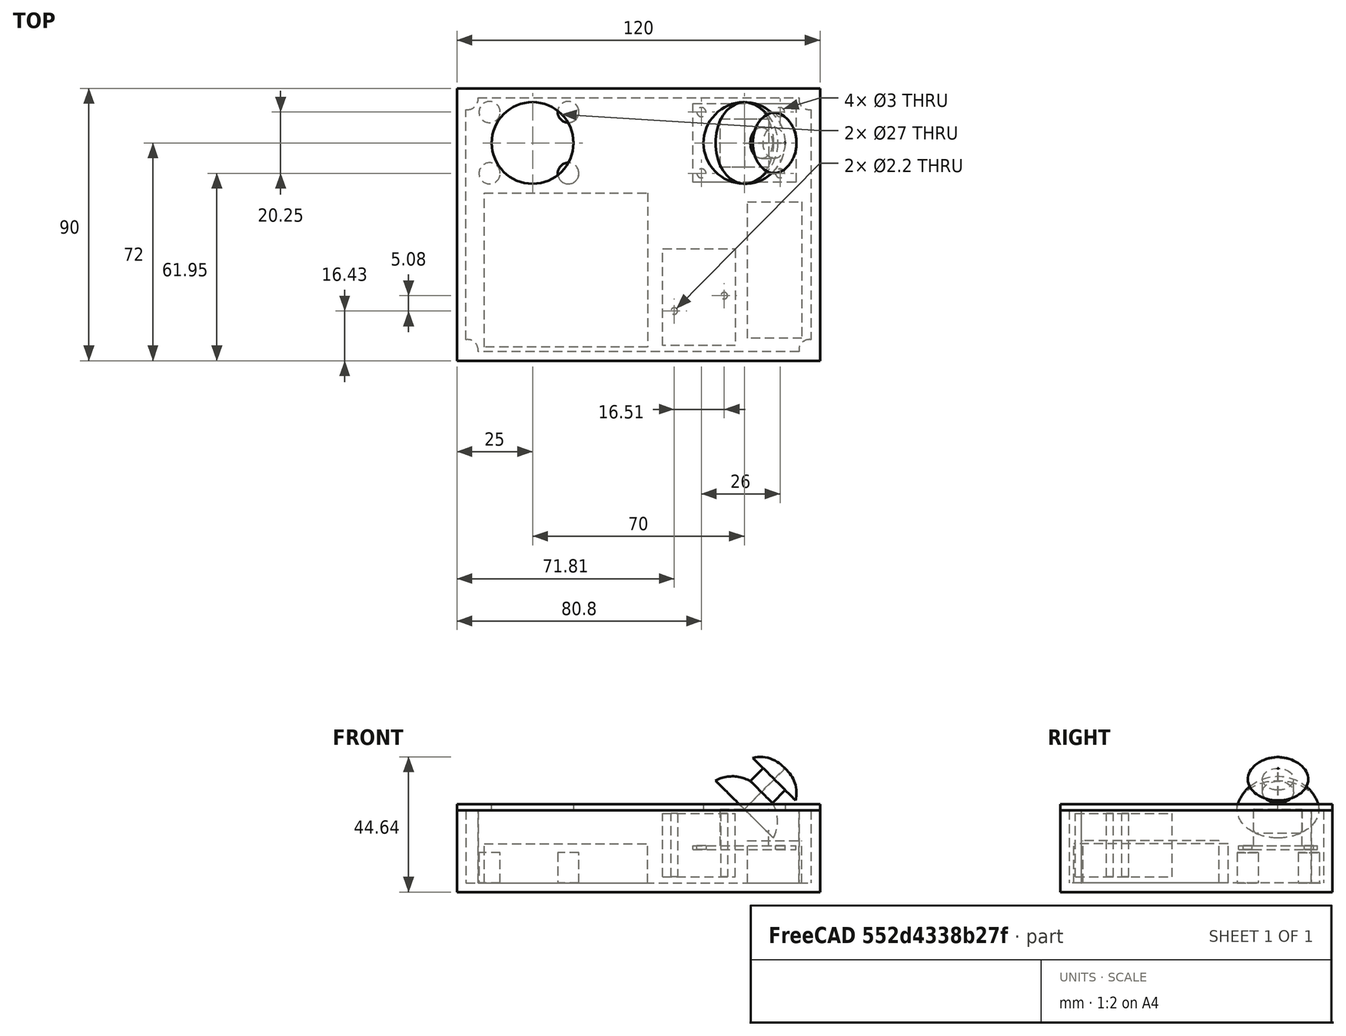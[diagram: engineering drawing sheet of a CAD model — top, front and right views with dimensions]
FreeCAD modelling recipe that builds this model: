
FCSTD DOCUMENT  (FreeCAD 0.18.4R)
Label: bottom
License: All rights reserved
LicenseURL: http://en.wikipedia.org/wiki/All_rights_reserved
objects: Sketcher::SketchObject×15, PartDesign::Pad×10, PartDesign::Body×7, PartDesign::ShapeBinder×6, TechDraw::DrawViewDimension×6, PartDesign::Pocket×4, TechDraw::DrawSVGTemplate×2, TechDraw::DrawViewPart×2, TechDraw::DrawPage×2, PartDesign::Plane×1, PartDesign::Revolution×1, PartDesign::FeatureBase×1
note: 60 computed .brp shape members not serialized (recipe doc carries the construction recipe); baked Part::Feature solids carry a one-line shape summary decoded from their .brp

FEATURE [PartDesign::Plane] DatumPlane
  Length = 140.785
  MapMode = 6
  ResizeMode = 0
  Width = 110.785
FEATURE [Sketcher::SketchObject] Sketch  label="body"
  MapMode = 5
  Support = -> [DatumPlane]
  sketch-geometry (7):
    g0: LineSegment StartX=-60 StartY=45 StartZ=0 EndX=60 EndY=45 EndZ=0
    g1: LineSegment StartX=60 StartY=45 StartZ=0 EndX=60 EndY=-45 EndZ=0
    g2: LineSegment StartX=60 StartY=-45 StartZ=0 EndX=-60 EndY=-45 EndZ=0
    g3: LineSegment StartX=-60 StartY=-45 StartZ=0 EndX=-60 EndY=45 EndZ=0
    g4: LineSegment [constr] StartX=-60 StartY=45 StartZ=0 EndX=60 EndY=-45 EndZ=0
    g5: LineSegment [constr] StartX=60 StartY=45 StartZ=0 EndX=-60 EndY=-45 EndZ=0
    g6: GeomPoint X=0 Y=0 Z=0
  constraints (17):
    c: Coincident(g0,g1)
    c: Coincident(g1,g2)
    c: Coincident(g2,g3)
    c: Coincident(g3,g0)
    c: Horizontal(g0)
    c: Horizontal(g2)
    c: Vertical(g1)
    c: Vertical(g3)
    c: DistanceX(g0,g0) = 120
    c: Coincident(g4,g1)
    c: Coincident(g5,g0)
    c: Coincident(g5,g2)
    c: PointOnObject(g6,g4)
    c: PointOnObject(g6,g5)
    c: Coincident(g6,g-1)
    c: DistanceY(g1,g1) = 90
    c: Coincident(g0,g4)
FEATURE [PartDesign::Pad] Pad
  Length = 27
  Length2 = 100
  Profile = -> Sketch
  Type = 0
FEATURE [Sketcher::SketchObject] Sketch001  label="hole"
  ExternalGeometry = -> [Sketch,Pad]
  MapMode = 5
  Placement = pos=(0,0,27) rot=(0,0,1;0rad)
  Support = -> [Pad]
  sketch-geometry (19):
    g0: LineSegment [constr] StartX=-60 StartY=45 StartZ=0 EndX=60 EndY=45 EndZ=0
    g1: LineSegment [constr] StartX=60 StartY=-45 StartZ=0 EndX=-60 EndY=-45 EndZ=0
    g2: LineSegment [constr] StartX=-60 StartY=-45 StartZ=0 EndX=-60 EndY=45 EndZ=0
    g3: Circle [constr] CenterX=-56.5 CenterY=41.5 CenterZ=0 NormalX=0 NormalY=0 NormalZ=1 AngleXU=0 Radius=3.5
    g4: Circle [constr] CenterX=56.5 CenterY=41.5 CenterZ=0 NormalX=0 NormalY=0 NormalZ=1 AngleXU=0 Radius=3.5
    g5: Circle [constr] CenterX=56.5 CenterY=-41.5 CenterZ=0 NormalX=0 NormalY=0 NormalZ=1 AngleXU=0 Radius=3.5
    g6: Circle [constr] CenterX=-56.5 CenterY=-41.5 CenterZ=0 NormalX=0 NormalY=0 NormalZ=1 AngleXU=0 Radius=3.5
    g7: LineSegment [constr] StartX=-57 StartY=42 StartZ=0 EndX=57 EndY=42 EndZ=0
    g8: LineSegment [constr] StartX=57 StartY=42 StartZ=0 EndX=57 EndY=-42 EndZ=0
    g9: LineSegment [constr] StartX=57 StartY=-42 StartZ=0 EndX=-57 EndY=-42 EndZ=0
    g10: LineSegment [constr] StartX=-57 StartY=-42 StartZ=0 EndX=-57 EndY=42 EndZ=0
    g11: ArcOfCircle CenterX=-56.5 CenterY=41.5 CenterZ=0 NormalX=0 NormalY=0 NormalZ=1 AngleXU=0 Radius=3.5 StartAngle=4.56904 EndAngle=6.42653
    g12: ArcOfCircle CenterX=56.5 CenterY=41.5 CenterZ=0 NormalX=0 NormalY=0 NormalZ=1 AngleXU=0 Radius=3.5 StartAngle=2.99825 EndAngle=4.85574
    g13: ArcOfCircle CenterX=56.5 CenterY=-41.5 CenterZ=0 NormalX=0 NormalY=0 NormalZ=1 AngleXU=0 Radius=3.5 StartAngle=1.42745 EndAngle=3.28494
    g14: LineSegment StartX=-53.0359 StartY=42 StartZ=0 EndX=53.0359 EndY=42 EndZ=0
    g15: LineSegment StartX=57 StartY=38.0359 StartZ=0 EndX=57 EndY=-38.0359 EndZ=0
    g16: ArcOfCircle CenterX=-56.5 CenterY=-41.5 CenterZ=0 NormalX=0 NormalY=0 NormalZ=1 AngleXU=0 Radius=3.5 StartAngle=6.13984 EndAngle=7.99733
    g17: LineSegment StartX=53.0359 StartY=-42 StartZ=0 EndX=-53.0359 EndY=-42 EndZ=0
    g18: LineSegment StartX=-57 StartY=-38.0359 StartZ=0 EndX=-57 EndY=38.0359 EndZ=0
  constraints (56):
    c: Coincident(g1,g2)
    c: Coincident(g2,g0)
    c: Tangent(g0,g3)
    c: Tangent(g3,g2)
    c: Radius(g3) = 3.5
    c: Tangent(g0,g4)
    c: Radius(g4) = 3.5
    c: Tangent(g5,g1)
    c: Radius(g5) = 3.5
    c: Radius(g6) = 3.5
    c: Tangent(g6,g1)
    c: Tangent(g6,g2)
    c: Coincident(g7,g8)
    c: Coincident(g8,g9)
    c: Coincident(g9,g10)
    c: Coincident(g10,g7)
    c: Horizontal(g7)
    c: Horizontal(g9)
    c: Vertical(g8)
    c: Vertical(g10)
    c: DistanceX(g0,g7) = 3
    c: DistanceY(g7,g0) = 3
    c: DistanceX(g8,g1) = 3
    c: DistanceY(g1,g8) = 3
    c: Coincident(g11,g3)
    c: PointOnObject(g11,g10)
    c: Coincident(g12,g4)
    c: PointOnObject(g12,g7)
    c: PointOnObject(g12,g8)
    c: Coincident(g13,g5)
    c: PointOnObject(g13,g8)
    c: PointOnObject(g13,g9)
    c: Radius(g11) = 3.5
    c: Radius(g12) = 3.5
    c: Radius(g13) = 3.5
    c: Coincident(g14,g11)
    c: Coincident(g14,g12)
    c: Horizontal(g14)
    c: Coincident(g15,g12)
    c: Coincident(g15,g13)
    c: Coincident(g16,g6)
    c: PointOnObject(g16,g10)
    c: PointOnObject(g16,g9)
    c: Coincident(g17,g13)
    c: Coincident(g17,g16)
    c: Coincident(g18,g16)
    c: Coincident(g18,g11)
    c: Radius(g16) = 3.5
    c: DistanceX(g12,g-3) = 3
    c: Coincident(g0,g-3)
    c: Coincident(g-3,g0)
    c: Tangent(g4,g-5)
    c: Coincident(g1,g-4)
    c: Coincident(g1,g-5)
    c: Coincident(g1,g-4)
    c: Tangent(g5,g-5)
FEATURE [PartDesign::Pocket] Pocket
  BaseFeature = -> Pad
  Length = 24
  Length2 = 100
  Profile = -> Sketch001
  Type = 0
FEATURE [Sketcher::SketchObject] Sketch006  label="pcb"
  MapMode = 5
  Support = -> [XY_Plane002]
  sketch-geometry (7):
    g0: LineSegment StartX=-17 StartY=13 StartZ=0 EndX=17 EndY=13 EndZ=0
    g1: LineSegment StartX=17 StartY=13 StartZ=0 EndX=17 EndY=-13 EndZ=0
    g2: LineSegment StartX=17 StartY=-13 StartZ=0 EndX=-17 EndY=-13 EndZ=0
    g3: LineSegment StartX=-17 StartY=-13 StartZ=0 EndX=-17 EndY=13 EndZ=0
    g4: LineSegment [constr] StartX=17 StartY=13 StartZ=0 EndX=-17 EndY=-13 EndZ=0
    g5: LineSegment [constr] StartX=-17 StartY=13 StartZ=0 EndX=17 EndY=-13 EndZ=0
    g6: GeomPoint X=0 Y=0 Z=0
  constraints (17):
    c: Coincident(g0,g1)
    c: Coincident(g1,g2)
    c: Coincident(g2,g3)
    c: Coincident(g3,g0)
    c: Horizontal(g0)
    c: Horizontal(g2)
    c: Vertical(g1)
    c: Vertical(g3)
    c: DistanceX(g0,g0) = 34
    c: DistanceY(g1,g1) = 26
    c: Coincident(g4,g0)
    c: Coincident(g4,g2)
    c: Coincident(g5,g0)
    c: Coincident(g5,g1)
    c: PointOnObject(g6,g4)
    c: PointOnObject(g6,g5)
    c: Coincident(g6,g-1)
FEATURE [PartDesign::Pad] Pad004
  Length = 1.35
  Length2 = 100
  Profile = -> Sketch006
  Type = 0
FEATURE [Sketcher::SketchObject] Sketch007  label="mounting_holes"
  ExternalGeometry = -> [Pad004]
  MapMode = 5
  Placement = pos=(0,0,1.35) rot=(0,0,1;0rad)
  Support = -> [Pad004]
  sketch-geometry (11):
    g0: Circle CenterX=-14.2 CenterY=10.2 CenterZ=0 NormalX=0 NormalY=0 NormalZ=1 AngleXU=0 Radius=1.5
    g1: Circle CenterX=11.8 CenterY=10.2 CenterZ=0 NormalX=0 NormalY=0 NormalZ=1 AngleXU=0 Radius=1.5
    g2: Circle CenterX=11.8 CenterY=-10.05 CenterZ=0 NormalX=0 NormalY=0 NormalZ=1 AngleXU=0 Radius=1.5
    g3: Circle CenterX=-14.2 CenterY=-10.05 CenterZ=0 NormalX=0 NormalY=0 NormalZ=1 AngleXU=0 Radius=1.5
    g4: LineSegment [constr] StartX=-15.7 StartY=13 StartZ=0 EndX=-15.7 EndY=-13 EndZ=0
    g5: LineSegment [constr] StartX=13.3 StartY=13 StartZ=0 EndX=13.3 EndY=-13 EndZ=0
    g6: LineSegment [constr] StartX=-15.7 StartY=-11.55 StartZ=0 EndX=13.3 EndY=-11.55 EndZ=0
    g7: LineSegment [constr] StartX=-15.7 StartY=11.7 StartZ=0 EndX=13.3 EndY=11.7 EndZ=0
    g8: GeomPoint X=0 Y=0 Z=0
    g9: LineSegment [constr] StartX=-17 StartY=13 StartZ=0 EndX=17 EndY=-13 EndZ=0
    g10: LineSegment [constr] StartX=17 StartY=13 StartZ=0 EndX=-17 EndY=-13 EndZ=0
  constraints (33):
    c: Diameter(g0) = 3
    c: Equal(g0,g1) = 3
    c: Equal(g0,g2) = 3
    c: Equal(g0,g3) = 3
    c: PointOnObject(g4,g-3)
    c: PointOnObject(g4,g-5)
    c: Vertical(g4)
    c: PointOnObject(g5,g-3)
    c: PointOnObject(g5,g-5)
    c: Vertical(g5)
    c: Tangent(g1,g5)
    c: Tangent(g2,g5)
    c: Tangent(g0,g4)
    c: Tangent(g3,g4)
    c: DistanceX(g4,g5) = 29
    c: PointOnObject(g6,g4)
    c: PointOnObject(g6,g5)
    c: Horizontal(g6)
    c: Tangent(g6,g3)
    c: PointOnObject(g7,g4)
    c: PointOnObject(g7,g5)
    c: Horizontal(g7)
    c: Tangent(g7,g0)
    c: Tangent(g1,g7)
    c: Tangent(g2,g6)
    c: DistanceY(g6,g7) = 23.25
    c: Coincident(g8,g-1)
    c: Coincident(g9,g-6)
    c: Coincident(g9,g-5)
    c: Coincident(g10,g-4)
    c: Coincident(g10,g-6)
    c: DistanceY(g7,g4) = 1.3
    c: DistanceX(g9,g7) = 1.3
FEATURE [PartDesign::Pocket] Pocket002
  BaseFeature = -> Pad004
  Length = 1.35
  Length2 = 100
  Profile = -> Sketch007
  Type = 0
FEATURE [Sketcher::SketchObject] Sketch008  label="potis"
  MapMode = 5
  Placement = pos=(0,0,1.35) rot=(0,0,1;0rad)
  Support = -> [Pocket002]
  sketch-geometry (7):
    g0: LineSegment StartX=-8 StartY=8 StartZ=0 EndX=8 EndY=8 EndZ=0
    g1: LineSegment StartX=8 StartY=8 StartZ=0 EndX=8 EndY=-8 EndZ=0
    g2: LineSegment StartX=8 StartY=-8 StartZ=0 EndX=-8 EndY=-8 EndZ=0
    g3: LineSegment StartX=-8 StartY=-8 StartZ=0 EndX=-8 EndY=8 EndZ=0
    g4: LineSegment [constr] StartX=-8 StartY=8 StartZ=0 EndX=8 EndY=-8 EndZ=0
    g5: LineSegment [constr] StartX=-8 StartY=-8 StartZ=0 EndX=8 EndY=8 EndZ=0
    g6: GeomPoint X=0 Y=0 Z=0
  constraints (17):
    c: Coincident(g0,g1)
    c: Coincident(g1,g2)
    c: Coincident(g2,g3)
    c: Coincident(g3,g0)
    c: Horizontal(g0)
    c: Horizontal(g2)
    c: Vertical(g1)
    c: Vertical(g3)
    c: DistanceX(g0,g0) = 16
    c: Equal(g0,g1)
    c: Coincident(g4,g0)
    c: Coincident(g4,g1)
    c: Coincident(g5,g2)
    c: Coincident(g5,g0)
    c: PointOnObject(g6,g4)
    c: PointOnObject(g6,g5)
    c: Coincident(g6,g-1)
FEATURE [PartDesign::Pad] Pad005
  BaseFeature = -> Pocket002
  Length = 12
  Length2 = 100
  Profile = -> Sketch008
  Type = 0
FEATURE [Sketcher::SketchObject] Sketch009  label="joy_hat"
  AttachmentOffset = pos=(0,0,0) rot=(1,0,0;1.5708rad)
  ExternalGeometry = -> [Pad005]
  MapMode = 2
  Placement = pos=(0,0,13.35) rot=(0.862856,0.357407,-0.357407;1.71777rad)
  sketch-geometry (11):
    g0: LineSegment StartX=0 StartY=0 StartZ=0 EndX=13.4918 EndY=0.0716788 EndZ=0
    g1: LineSegment [constr] StartX=0 StartY=0 StartZ=0 EndX=-0.0425023 EndY=8 EndZ=0
    g2: LineSegment [constr] StartX=-0.0425023 StartY=8 StartZ=0 EndX=5.0875 EndY=8.02725 EndZ=0
    g3: LineSegment StartX=5.0875 StartY=8.02725 StartZ=0 EndX=5.05562 EndY=14.0273 EndZ=0
    g4: LineSegment [constr] StartX=-0.074379 StartY=14 StartZ=0 EndX=9.92562 EndY=14.0531 EndZ=0
    g5: LineSegment [constr] StartX=-0.0425023 StartY=8 StartZ=0 EndX=-0.074379 EndY=14 EndZ=0
    g6: LineSegment [constr] StartX=-0.074379 StartY=14 StartZ=0 EndX=0 EndY=19 EndZ=0
    g7: LineSegment StartX=5.05562 StartY=14.0273 StartZ=0 EndX=9.92562 EndY=14.0531 EndZ=0
    g8: ArcOfCircle CenterX=0.937498 CenterY=8.45 CenterZ=0 NormalX=0 NormalY=0 NormalZ=1 AngleXU=0 Radius=10.5916 StartAngle=0.557442 EndAngle=1.65943
    g9: ArcOfCircle CenterX=2.2 CenterY=-3.44 CenterZ=0 NormalX=0 NormalY=0 NormalZ=1 AngleXU=0 Radius=11.8252 StartAngle=0.301513 EndAngle=1.32412
    g10: LineSegment StartX=0 StartY=19 StartZ=0 EndX=0 EndY=0 EndZ=0
  constraints (31):
    c: Coincident(g3,g7)
    c: Perpendicular(g0,g1)
    c: DistanceY(g1,g1) = 8
    c: DistanceY(g5,g5) = 6
    c: DistanceY(g6,g6) = 5
    c: Perpendicular(g3,g4)
    c: DistanceX(g2,g2) = 5.13
    c: DistanceX(g4,g4) = 10
    c: Perpendicular(g2,g1)
    c: Coincident(g1,g2)
    c: Coincident(g1,g5)
    c: Coincident(g4,g5)
    c: Coincident(g4,g6)
    c: Coincident(g4,g7)
    c: Coincident(g0,g1)
    c: Perpendicular(g7,g3)
    c: Coincident(g8,g6)
    c: Coincident(g8,g7)
    c: Coincident(g9,g3)
    c: Coincident(g9,g0)
    c: Coincident(g2,g3)
    c: Perpendicular(g3,g2)
    c: DistanceY(g9,g0) = 3.44
    c: DistanceX(g0,g9) = 2.2
    c: DistanceX(g1,g8) = 0.98
    c: DistanceY(g1,g8) = 0.45
    c: Coincident(g0,g-1)
    c: Perpendicular(g5,g2)
    c: Vertical(g10)
    c: Coincident(g10,g8)
    c: Coincident(g0,g10)
FEATURE [PartDesign::Revolution] Revolution
  Angle = 360
  Axis = (5.6268,1.6e-15,5.68691)
  Base = (0,0,13.35)
  BaseFeature = -> Pad005
  Profile = -> Sketch009
  ReferenceAxis = -> Sketch009 [Axis0]
  Reversed = true
FEATURE [PartDesign::Body] Body002  label="joy_left_orig"
  Group = -> [Sketch006,Pad004,Sketch007,Pocket002,Sketch008,Pad005,Sketch009,Revolution]
  Origin = -> Origin002
  Placement = pos=(-35,27,14) rot=(0,0,1;0rad)
  Tip = -> Revolution
FEATURE [PartDesign::ShapeBinder] ShapeBinder  label="shapebinder_pcb_holes_joy_left"
  Placement = pos=(-35,27,14) rot=(0,0,1;0rad)
  Support = -> [Pocket002]
  TraceSupport = true
FEATURE [Sketcher::SketchObject] Sketch010  label="mounts_joy_left"
  ExternalGeometry = -> [ShapeBinder]
  MapMode = 5
  Placement = pos=(0,0,3) rot=(0,0,1;0rad)
  Support = -> [Pocket]
  sketch-geometry (4):
    g0: Circle CenterX=-49.2 CenterY=37.2 CenterZ=0 NormalX=0 NormalY=0 NormalZ=1 AngleXU=0 Radius=3.5
    g1: Circle CenterX=-23.2 CenterY=37.2 CenterZ=0 NormalX=0 NormalY=0 NormalZ=1 AngleXU=0 Radius=3.5
    g2: Circle CenterX=-23.2 CenterY=16.95 CenterZ=0 NormalX=0 NormalY=0 NormalZ=1 AngleXU=0 Radius=3.5
    g3: Circle CenterX=-49.2 CenterY=16.95 CenterZ=0 NormalX=0 NormalY=0 NormalZ=1 AngleXU=0 Radius=3.5
  constraints (8):
    c: Diameter(g0) = 7
    c: Coincident(g0,g-3)
    c: Equal(g0,g1) = 7
    c: Coincident(g1,g-4)
    c: Equal(g0,g2) = 7
    c: Coincident(g2,g-5)
    c: Equal(g0,g3) = 7
    c: Coincident(g3,g-6)
FEATURE [PartDesign::Pad] Pad006
  BaseFeature = -> Pocket
  Length = 10
  Length2 = 100
  Profile = -> Sketch010
  Type = 0
FEATURE [PartDesign::FeatureBase] Clone
  BaseFeature = -> Body002
  Placement = pos=(0,0,9) rot=(0,0,1;0rad)
FEATURE [PartDesign::Body] Body003  label="joy_right_cloned"
  BaseFeature = -> Body002
  Group = -> [Clone]
  Origin = -> Origin003
  Placement = pos=(35,27,5) rot=(0,0,1;0rad)
  Tip = -> Clone
FEATURE [PartDesign::ShapeBinder] ShapeBinder001  label="shapebinder_pcb_holes_joy_right"
  Placement = pos=(35,27,5) rot=(0,0,1;0rad)
  Support = -> [Clone]
  TraceSupport = true
FEATURE [Sketcher::SketchObject] Sketch011  label="mounts_joy_right"
  ExternalGeometry = -> [ShapeBinder001]
  MapMode = 5
  Placement = pos=(0,0,3) rot=(0,0,1;0rad)
  Support = -> [Pad006]
  sketch-geometry (4):
    g0: Circle CenterX=20.8 CenterY=37.2 CenterZ=0 NormalX=0 NormalY=0 NormalZ=1 AngleXU=0 Radius=3.5
    g1: Circle CenterX=46.8 CenterY=37.2 CenterZ=0 NormalX=0 NormalY=0 NormalZ=1 AngleXU=0 Radius=3.5
    g2: Circle CenterX=46.8 CenterY=16.95 CenterZ=0 NormalX=0 NormalY=0 NormalZ=1 AngleXU=0 Radius=3.5
    g3: Circle CenterX=20.8 CenterY=16.95 CenterZ=0 NormalX=0 NormalY=0 NormalZ=1 AngleXU=0 Radius=3.5
  constraints (8):
    c: Coincident(g0,g-5)
    c: Diameter(g0) = 7
    c: Equal(g0,g1) = 7
    c: Coincident(g1,g-6)
    c: Equal(g0,g2) = 7
    c: Coincident(g2,g-4)
    c: Equal(g0,g3) = 7
    c: Coincident(g3,g-3)
FEATURE [PartDesign::Pad] Pad007
  BaseFeature = -> Pad006
  Length = 10
  Length2 = 100
  Profile = -> Sketch011
  Type = 0
FEATURE [PartDesign::ShapeBinder] ShapeBinder002  label="shapebinder_lid"
  Support = -> [Pocket]
  TraceSupport = false
FEATURE [Sketcher::SketchObject] Sketch012  label="lid"
  ExternalGeometry = -> [ShapeBinder002]
  MapMode = 5
  Placement = pos=(0,0,27) rot=(0,0,1;0rad)
  Support = -> [ShapeBinder002]
  sketch-geometry (4):
    g0: LineSegment StartX=-60 StartY=45 StartZ=0 EndX=60 EndY=45 EndZ=0
    g1: LineSegment StartX=60 StartY=45 StartZ=0 EndX=60 EndY=-45 EndZ=0
    g2: LineSegment StartX=60 StartY=-45 StartZ=0 EndX=-60 EndY=-45 EndZ=0
    g3: LineSegment StartX=-60 StartY=-45 StartZ=0 EndX=-60 EndY=45 EndZ=0
  constraints (10):
    c: Coincident(g0,g1)
    c: Coincident(g1,g2)
    c: Coincident(g2,g3)
    c: Coincident(g3,g0)
    c: Horizontal(g0)
    c: Horizontal(g2)
    c: Vertical(g1)
    c: Vertical(g3)
    c: Coincident(g0,g-5)
    c: Coincident(g1,g-6)
FEATURE [PartDesign::Pad] Pad008
  Length = 2
  Length2 = 100
  Profile = -> Sketch012
  Type = 0
FEATURE [PartDesign::ShapeBinder] ShapeBinder003  label="shapebinder_joy_left"
  Placement = pos=(-35,27,14) rot=(0,0,1;0rad)
  Support = -> [Revolution]
  TraceSupport = true
FEATURE [PartDesign::ShapeBinder] ShapeBinder004  label="shapebinder_joy_right"
  Placement = pos=(35,27,14) rot=(0,0,1;0rad)
  Support = -> [Clone]
  TraceSupport = true
FEATURE [Sketcher::SketchObject] Sketch013  label="lid_joystick_holes"
  ExternalGeometry = -> [ShapeBinder003,ShapeBinder004]
  MapMode = 5
  Placement = pos=(0,0,29) rot=(0,0,1;0rad)
  Support = -> [Pad008]
  sketch-geometry (8):
    g0: LineSegment [constr] StartX=-43 StartY=35 StartZ=0 EndX=-27 EndY=19 EndZ=0
    g1: LineSegment [constr] StartX=-27 StartY=35 StartZ=0 EndX=-43 EndY=19 EndZ=0
    g2: GeomPoint X=-35 Y=27 Z=0
    g3: LineSegment [constr] StartX=27 StartY=35 StartZ=0 EndX=43 EndY=19 EndZ=0
    g4: LineSegment [constr] StartX=43 StartY=35 StartZ=0 EndX=27 EndY=19 EndZ=0
    g5: GeomPoint X=35 Y=27 Z=0
    g6: Circle CenterX=-35 CenterY=27 CenterZ=0 NormalX=0 NormalY=0 NormalZ=1 AngleXU=0 Radius=13.5
    g7: Circle CenterX=35 CenterY=27 CenterZ=0 NormalX=0 NormalY=0 NormalZ=1 AngleXU=0 Radius=13.5
  constraints (16):
    c: Coincident(g0,g-4)
    c: Coincident(g0,g-6)
    c: Coincident(g1,g-5)
    c: PointOnObject(g2,g0)
    c: PointOnObject(g2,g1)
    c: Coincident(g3,g-10)
    c: Coincident(g3,g-9)
    c: Coincident(g4,g-8)
    c: Coincident(g4,g-10)
    c: PointOnObject(g5,g3)
    c: PointOnObject(g5,g4)
    c: Coincident(g-6,g1)
    c: Coincident(g6,g2)
    c: Diameter(g6) = 27
    c: Equal(g6,g7) = 27
    c: Coincident(g7,g5)
FEATURE [PartDesign::Pocket] Pocket003
  BaseFeature = -> Pad008
  Length = 2
  Length2 = 100
  Profile = -> Sketch013
  Type = 0
FEATURE [PartDesign::Body] Body004  label="case_top"
  Group = -> [ShapeBinder002,Sketch012,Pad008,ShapeBinder003,ShapeBinder004,Sketch013,Pocket003]
  Origin = -> Origin004
  Tip = -> Pocket003
FEATURE [Sketcher::SketchObject] Sketch014  label="pcb001"
  MapMode = 5
  Support = -> [XY_Plane005]
  sketch-geometry (7):
    g0: LineSegment StartX=-12 StartY=16 StartZ=0 EndX=12 EndY=16 EndZ=0
    g1: LineSegment StartX=12 StartY=16 StartZ=0 EndX=12 EndY=-16 EndZ=0
    g2: LineSegment StartX=12 StartY=-16 StartZ=0 EndX=-12 EndY=-16 EndZ=0
    g3: LineSegment StartX=-12 StartY=-16 StartZ=0 EndX=-12 EndY=16 EndZ=0
    g4: LineSegment [constr] StartX=-12 StartY=16 StartZ=0 EndX=12 EndY=-16 EndZ=0
    g5: LineSegment [constr] StartX=-12 StartY=-16 StartZ=0 EndX=12 EndY=16 EndZ=0
    g6: GeomPoint X=0 Y=0 Z=0
  constraints (17):
    c: Coincident(g0,g1)
    c: Coincident(g1,g2)
    c: Coincident(g2,g3)
    c: Coincident(g3,g0)
    c: Horizontal(g0)
    c: Horizontal(g2)
    c: Vertical(g1)
    c: Vertical(g3)
    c: DistanceX(g0,g0) = 24
    c: DistanceY(g1,g1) = 32
    c: Coincident(g4,g0)
    c: Coincident(g4,g1)
    c: Coincident(g5,g2)
    c: Coincident(g5,g0)
    c: PointOnObject(g6,g4)
    c: PointOnObject(g6,g5)
    c: Coincident(g6,g-1)
FEATURE [PartDesign::Pad] Pad009
  Length = 21
  Length2 = 100
  Profile = -> Sketch014
  Type = 0
FEATURE [Sketcher::SketchObject] Sketch015  label="mounting_holes001"
  ExternalGeometry = -> [Pad009]
  MapMode = 5
  Placement = pos=(0,0,21) rot=(0,0,1;0rad)
  Support = -> [Pad009]
  sketch-geometry (2):
    g0: Circle CenterX=-8.19 CenterY=-4.57 CenterZ=0 NormalX=0 NormalY=0 NormalZ=1 AngleXU=0 Radius=1.1
    g1: Circle CenterX=8.32 CenterY=0.51 CenterZ=0 NormalX=0 NormalY=0 NormalZ=1 AngleXU=0 Radius=1.1
  constraints (6):
    c: Diameter(g0) = 2.2
    c: Equal(g0,g1) = 2.2
    c: Distance(g0,g-4) = 3.81
    c: Distance(g0,g-3) = 11.43
    c: Distance(g1,g-3) = 16.51
    c: Distance(g1,g-4) = 20.32
FEATURE [PartDesign::Pocket] Pocket004
  BaseFeature = -> Pad009
  Length = 21
  Length2 = 100
  Profile = -> Sketch015
  Type = 0
FEATURE [PartDesign::Body] Body005  label="power pcb"
  Group = -> [Sketch014,Pad009,Sketch015,Pocket004]
  Origin = -> Origin005
  Placement = pos=(20,-24,5) rot=(0,0,1;0rad)
  Tip = -> Pocket004
FEATURE [Sketcher::SketchObject] Sketch016
  MapMode = 5
  Support = -> [XY_Plane006]
  sketch-geometry (7):
    g0: LineSegment StartX=-27 StartY=25.5 StartZ=0 EndX=27 EndY=25.5 EndZ=0
    g1: LineSegment StartX=27 StartY=25.5 StartZ=0 EndX=27 EndY=-25.5 EndZ=0
    g2: LineSegment StartX=27 StartY=-25.5 StartZ=0 EndX=-27 EndY=-25.5 EndZ=0
    g3: LineSegment StartX=-27 StartY=-25.5 StartZ=0 EndX=-27 EndY=25.5 EndZ=0
    g4: LineSegment [constr] StartX=-27 StartY=25.5 StartZ=0 EndX=27 EndY=-25.5 EndZ=0
    g5: LineSegment [constr] StartX=27 StartY=25.5 StartZ=0 EndX=-27 EndY=-25.5 EndZ=0
    g6: GeomPoint X=0 Y=0 Z=0
  constraints (17):
    c: Coincident(g0,g1)
    c: Coincident(g1,g2)
    c: Coincident(g2,g3)
    c: Coincident(g3,g0)
    c: Horizontal(g0)
    c: Horizontal(g2)
    c: Vertical(g1)
    c: Vertical(g3)
    c: DistanceX(g2,g2) = 54
    c: DistanceY(g1,g1) = 51
    c: Coincident(g4,g0)
    c: Coincident(g4,g1)
    c: Coincident(g5,g0)
    c: Coincident(g5,g2)
    c: PointOnObject(g6,g4)
    c: PointOnObject(g6,g5)
    c: Coincident(g6,g-1)
FEATURE [PartDesign::Pad] Pad010
  Length = 13
  Length2 = 100
  Profile = -> Sketch016
  Type = 0
FEATURE [PartDesign::Body] Body006  label="battery_holder"
  Group = -> [Sketch016,Pad010]
  Origin = -> Origin006
  Placement = pos=(-24,-15,3) rot=(0,0,1;0rad)
  Tip = -> Pad010
FEATURE [PartDesign::ShapeBinder] ShapeBinder005  label="shapebinder_power_pcb_holes"
  Placement = pos=(20,-24,5) rot=(0,0,1;0rad)
  Support = -> [Pocket004]
  TraceSupport = true
FEATURE [Sketcher::SketchObject] Sketch017  label="power_pcb_mounts"
  ExternalGeometry = -> [ShapeBinder005]
  MapMode = 5
  Placement = pos=(0,0,3) rot=(0,0,1;0rad)
  Support = -> [Pad007]
  sketch-geometry (2):
    g0: Circle CenterX=11.81 CenterY=-28.57 CenterZ=0 NormalX=0 NormalY=0 NormalZ=1 AngleXU=0 Radius=2.5
    g1: Circle CenterX=28.32 CenterY=-23.49 CenterZ=0 NormalX=0 NormalY=0 NormalZ=1 AngleXU=0 Radius=2.5
  constraints (4):
    c: Diameter(g0) = 5
    c: Coincident(g0,g-4)
    c: Equal(g0,g1) = 5
    c: Coincident(g1,g-3)
FEATURE [PartDesign::Pad] Pad011
  BaseFeature = -> Pad007
  Length = 5
  Length2 = 100
  Profile = -> Sketch017
  Type = 0
FEATURE [PartDesign::Body] Body  label="case_bottom"
  Group = -> [DatumPlane,Sketch,Pad,Sketch001,Pocket,ShapeBinder,Sketch010,Pad006,ShapeBinder001,Sketch011,Pad007,ShapeBinder005,Sketch017,Pad011]
  Origin = -> Origin
  Tip = -> Pad006
FEATURE [Sketcher::SketchObject] Sketch018  label="pcb002"
  MapMode = 5
  sketch-geometry (7):
    g0: LineSegment StartX=-9 StartY=22.5 StartZ=0 EndX=9 EndY=22.5 EndZ=0
    g1: LineSegment StartX=9 StartY=22.5 StartZ=0 EndX=9 EndY=-22.5 EndZ=0
    g2: LineSegment StartX=9 StartY=-22.5 StartZ=0 EndX=-9 EndY=-22.5 EndZ=0
    g3: LineSegment StartX=-9 StartY=-22.5 StartZ=0 EndX=-9 EndY=22.5 EndZ=0
    g4: LineSegment [constr] StartX=-9 StartY=22.5 StartZ=0 EndX=9 EndY=-22.5 EndZ=0
    g5: LineSegment [constr] StartX=9 StartY=22.5 StartZ=0 EndX=-9 EndY=-22.5 EndZ=0
    g6: GeomPoint X=0 Y=0 Z=0
  constraints (17):
    c: Coincident(g0,g1)
    c: Coincident(g1,g2)
    c: Coincident(g2,g3)
    c: Coincident(g3,g0)
    c: Horizontal(g0)
    c: Horizontal(g2)
    c: Vertical(g1)
    c: Vertical(g3)
    c: DistanceY(g3,g3) = 45
    c: DistanceX(g2,g2) = 18
    c: Coincident(g5,g0)
    c: Coincident(g5,g2)
    c: PointOnObject(g6,g4)
    c: PointOnObject(g6,g5)
    c: Coincident(g0,g4)
    c: Coincident(g1,g4)
    c: Coincident(g6,g-1)
FEATURE [PartDesign::Pad] Pad012
  Length = 14
  Length2 = 100
  Profile = -> Sketch018
  Type = 0
FEATURE [PartDesign::Body] Body007  label="arduino_nano"
  Group = -> [Sketch018,Pad012]
  Origin = -> Origin007
  Placement = pos=(45,-15,3) rot=(0,0,1;0rad)
  Tip = -> Pad012
FEATURE [TechDraw::DrawSVGTemplate] Template
  EditableTexts = Designed_by_Name=Designed by Name; Drawing_number=Drawing number; FC-Date=Date; FC-SC=Scale; FC-SH=Sheet; FC-Title=Title; Subtitle=Subtitle; Weight=Weight
  Height = 210
  Orientation = 1
  Width = 297
FEATURE [TechDraw::DrawViewPart] View001  label="view_top"
  CoarseView = false
  Direction = (0,0,1)
  Focus = 100
  HardHidden = false
  IsoCount = 0
  IsoHidden = false
  IsoVisible = false
  LockPosition = false
  Perspective = false
  Rotation = 0
  ScaleType = 0
  SeamHidden = false
  SeamVisible = false
  SmoothHidden = false
  SmoothVisible = false
  Source = -> [Body]
  X = 102.679
  Y = 138.825
FEATURE [TechDraw::DrawViewDimension] Dimension
  Arbitrary = false
  FormatSpec = %.2f
  LockPosition = false
  MeasureType = 1
  OverTolerance = 0
  References2D = -> [View001]
  Rotation = 0
  ScaleType = 0
  Type = 1
  UnderTolerance = 0
  X = 0
  Y = 58.2347
FEATURE [TechDraw::DrawViewDimension] Dimension001
  Arbitrary = false
  FormatSpec = %.2f
  LockPosition = false
  MeasureType = 1
  OverTolerance = 0
  References2D = -> [View001]
  Rotation = 0
  ScaleType = 0
  Type = 2
  UnderTolerance = 0
  X = -91.0611
  Y = -0.810289
FEATURE [TechDraw::DrawViewDimension] Dimension002
  Arbitrary = false
  FormatSpec = ⌀%.2f
  LockPosition = false
  MeasureType = 1
  OverTolerance = 0
  References2D = -> [View001]
  Rotation = 0
  ScaleType = 0
  Type = 5
  UnderTolerance = 0
  X = -73.4662
  Y = 34.8424
FEATURE [TechDraw::DrawViewDimension] Dimension003
  Arbitrary = false
  FormatSpec = ⌀%.2f
  LockPosition = false
  MeasureType = 1
  OverTolerance = 0
  References2D = -> [View001]
  Rotation = 0
  ScaleType = 0
  Type = 5
  UnderTolerance = 0
  X = 75.4072
  Y = 1.23282
FEATURE [TechDraw::DrawPage] Page
  KeepUpdated = true
  ProjectionType = 0
  Template = -> Template
  Views = -> [View001,Dimension,Dimension001,Dimension002,Dimension003]
FEATURE [TechDraw::DrawSVGTemplate] Template001
  EditableTexts = Designed_by_Name=Designed by Name; Drawing_number=Drawing number; FC-Date=Date; FC-SC=Scale; FC-SH=Sheet; FC-Title=Title; Subtitle=Subtitle; Weight=Weight
  Height = 210
  Orientation = 1
  Width = 297
FEATURE [TechDraw::DrawViewPart] View
  CoarseView = false
  Direction = (0,-1,0)
  Focus = 100
  HardHidden = false
  IsoCount = 0
  IsoHidden = false
  IsoVisible = false
  LockPosition = false
  Perspective = false
  Rotation = 0
  ScaleType = 0
  SeamHidden = false
  SeamVisible = false
  SmoothHidden = false
  SmoothVisible = false
  Source = -> [Body,Body002,Body003,Body004]
  X = 125.992
  Y = 157.669
FEATURE [TechDraw::DrawViewDimension] Dimension004
  Arbitrary = false
  FormatSpec = %.2f
  LockPosition = false
  MeasureType = 1
  OverTolerance = 0
  References2D = -> [View]
  Rotation = 0
  ScaleType = 0
  Type = 2
  UnderTolerance = 0
  X = 60
  Y = -8.81779
FEATURE [TechDraw::DrawViewDimension] Dimension005
  Arbitrary = false
  FormatSpec = %.2f
  LockPosition = false
  MeasureType = 1
  OverTolerance = 0
  References2D = -> [View]
  Rotation = 0
  ScaleType = 0
  Type = 2
  UnderTolerance = 0
  X = -74.7356
  Y = 5.7133
FEATURE [TechDraw::DrawPage] Page001
  KeepUpdated = true
  ProjectionType = 0
  Template = -> Template001
  Views = -> [View,Dimension004,Dimension005]
